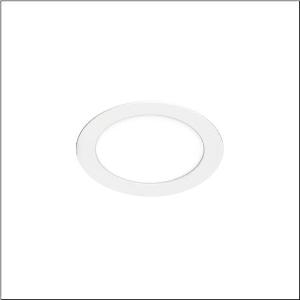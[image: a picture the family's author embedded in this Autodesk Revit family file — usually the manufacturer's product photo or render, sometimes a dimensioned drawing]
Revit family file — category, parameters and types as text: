
# Revit family: lunis_41_flat_51dr107fgca
name_source: partatom
category: Lighting Fixtures
units: mm (PartAtom-declared; Revit-internal decimal feet)

## family parameters
Cut with Voids When Loaded = No
Host = Face
Light Source = No
Part Type = Normal
Room Calculation Point = No
Round Connector Dimension = Use Diameter
Shared = No

## types (1)
- --- (1 x LED, 2160 lm, 22 W, 4000K)
    Apparent Load = 22 VA
    CIE Flux Codes = 49 80 96 100 100
    Color Rendering = 80
    Color Temperature = 4000K
    Default Elevation = 1800 mm
    Description = Lunis 41,  flat, downlight, light emission: direct distribution, LED rated luminous flux: 2.050lm, light colour: 830/840, control gear: ECG, mains connection: 230V, AC, 50/60Hz, housing, round, of aluminium, coated, traffic white (RAL 9016), diameter: 225mm, protection rating (complete): IP20, protection rating (on room side): IP44, insulation class (complete): insulation class II (safety insulation), certification: CE, permissible ambient temperature for indoor applications: -20..+40°C, packaging unit: 1 piece
    Height = 0 mm  [stored 0 ft]
    Lamp = 1 x LED
    Lamp Light Flux = 2160 lm
    Lamp Power = 22 W
    Lamp count = 1
    Length = 225 mm
    Luminous efficacy = 98 lm/W
    Manufacturer = Siteco
    ModVariant = No
    Model = 51DR107FGCA
    Mounting Place = Ceiling
    Mounting Type = Recessed
    Number of Poles = 1
    OnlyDefault = Yes
    Power Factor = 1
    Product Name = Lunis 41 flat
    Product group = downlight
    ProductGroupID = 401
    Protection Class = Protection class II
    Protection Degree = IP 20
    RLX_Detail_Level = 1
    RLX_Emergency_Light_Flux = 0 lm
    RLX_Emergency_Type = 0
    RLX_Emergency_Type_DB = No
    RlxData = <blob elided: 22061 chars, md5=b79bf6d3>
    Socket = socket
    Standby Power = 0 W
    System Light Flux = 2160 lm
    System Power = 22 W
    Type Comments = factory setting: colour temperature 4000K
    Type Image = l_1007032.jpg
    URL = http://relux.com
    VarID = @adj_168263
    Voltage = 0 V
    Weight = 0.00 kg
    Width = 0 mm  [stored 0 ft]

note: [stored X ft] marks values corroborated as IEEE doubles in the binary element streams (Revit-internal decimal feet)

## geometry (parser evidence)
native form markers: Blend x4, Sweep x11
no freeform markers — native parametric forms only
